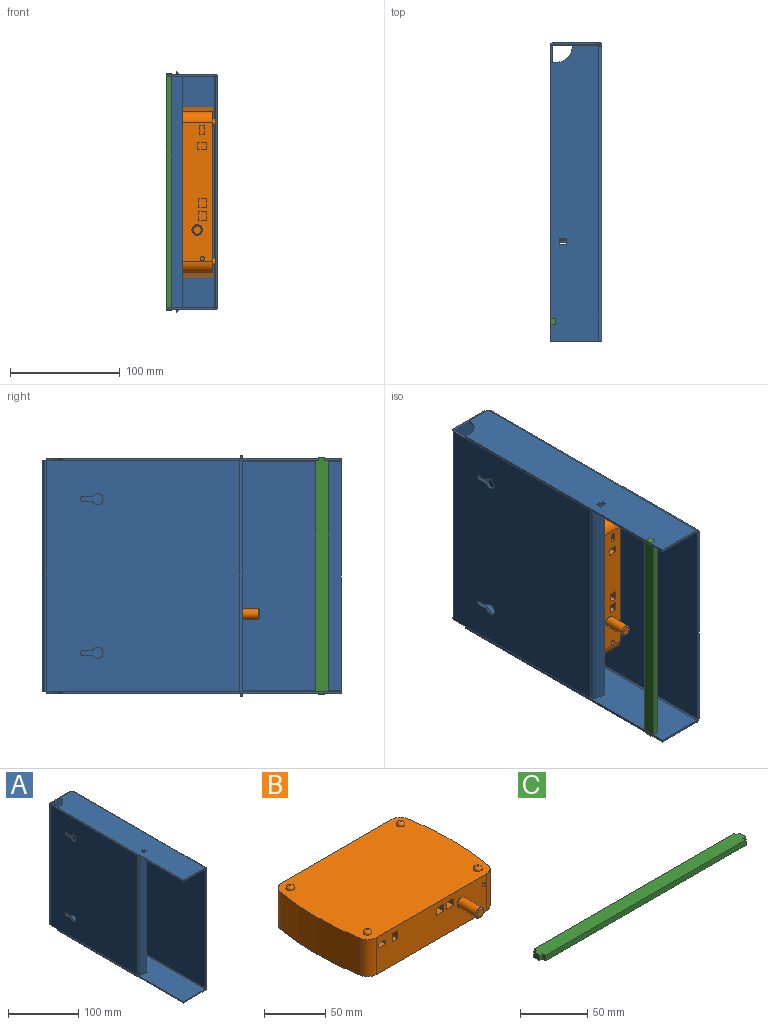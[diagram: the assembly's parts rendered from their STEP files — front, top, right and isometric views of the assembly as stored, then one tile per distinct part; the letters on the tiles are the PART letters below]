
ASSEMBLY  parts=3 mates=4
PART A: 83 faces, bbox 47x272x220 mm
  f0: plane 269x208mm, normal (1,0,0), area 55952.6mm2, adj f1,f3,f4,f49,f65,f81
  f1: plane 208x2mm, normal (0,-1,0), area 416mm2, adj f0,f2,f63,f79
  f2: plane 269x208mm, normal (-1,0,0), area 55952.6mm2, adj f1,f3,f4,f50,f66,f82
  f3: cylinder r=2.5mm len=2mm, axis (-1,0,0), area 1.5mm2, adj f0,f2,f47,f80
  f4: cylinder r=2.5mm len=2mm, axis (-1,0,0), area 1.5mm2, adj f0,f2,f48,f64
  f5: plane 40.04x2mm, normal (0,0,1), area 80.1mm2, adj f7,f11,f12,f44
  f6: plane 40.04x2mm, normal (0,0,-1), area 80.1mm2, adj f7,f11,f13,f43
  f7: plane 210x41mm, normal (0,1,0), area 8078mm2, adj f5,f6,f8,f9,f10,f12,f13,f45
  f8: cylinder r=7.5mm len=15mm, axis (0,1,0), area 94.2mm2, adj f7,f11
  f9: cylinder r=7.5mm len=15mm, axis (0,1,0), area 94.2mm2, adj f7,f11
  f10: cylinder r=7.5mm len=15mm, axis (0,1,0), area 94.2mm2, adj f7,f11
  f11: plane 210x41mm, normal (0,-1,0), area 8078mm2, adj f5,f6,f8,f9,f10,f12,f13,f46
  f12: cylinder r=2.5mm len=2mm, axis (0,-1,0), area 3.7mm2, adj f5,f7,f11,f47
  f13: cylinder r=2.5mm len=2mm, axis (0,-1,0), area 3.7mm2, adj f6,f7,f11,f48
  f14: plane 6.88x2mm, normal (0,0,-1), area 13.8mm2, adj f15,f27,f28,f29
  f15: cylinder r=5mm len=3.57mm, axis (-1,0,0), area 8mm2, adj f14,f16,f28,f29
  f16: cylinder r=5mm len=10mm, axis (-1,0,0), area 47.3mm2, adj f15,f17,f28,f29
  f17: cylinder r=5mm len=3.57mm, axis (-1,0,0), area 8mm2, adj f16,f18,f28,f29
  f18: plane 6.78x2mm, normal (0,0,1), area 13.6mm2, adj f17,f27,f28,f29
  f19: plane 6.78x2mm, normal (0,0,-1), area 13.6mm2, adj f20,f26,f28,f29
  f20: cylinder r=5mm len=3.57mm, axis (-1,0,0), area 8mm2, adj f19,f21,f28,f29
  f21: cylinder r=5mm len=10mm, axis (-1,0,0), area 47.3mm2, adj f20,f22,f28,f29
  f22: cylinder r=5mm len=3.57mm, axis (-1,0,0), area 8mm2, adj f21,f23,f28,f29
  f23: plane 6.88x2mm, normal (0,0,1), area 13.8mm2, adj f22,f26,f28,f29
  f24: plane 176x2mm, normal (0,0,1), area 352mm2, adj f28,f29,f40,f44
  f25: plane 176x2mm, normal (0,0,-1), area 352mm2, adj f28,f29,f39,f43
  f26: cylinder r=2mm len=4mm, axis (-1,0,0), area 12.8mm2, adj f19,f23,f28,f29
  f27: cylinder r=2mm len=4mm, axis (-1,0,0), area 12.8mm2, adj f14,f18,f28,f29
  f28: plane 210x176mm, normal (-1,0,0), area 36713.9mm2, adj f14,f15,f16,f17,f18,f19,f20,f21
  f29: plane 210x176mm, normal (1,0,0), area 36713.9mm2, adj f14,f15,f16,f17,f18,f19,f20,f21
  f30: plane 5x2mm, normal (-1,0,0), area 10mm2, adj f31,f36,f37,f38
  f31: plane 6x5mm, normal (0.64,0,-0.77), area 15.6mm2, adj f30,f32,f37,f38
  f32: plane 210x2mm, normal (1,0,0), area 420mm2, adj f31,f33,f37,f38
  f33: plane 6x5mm, normal (0.64,0,0.77), area 15.6mm2, adj f32,f34,f37,f38
  f34: plane 5x2mm, normal (-1,0,0), area 10mm2, adj f33,f35,f37,f38
  f35: plane 6x2mm, normal (0,0,1), area 12mm2, adj f34,f37,f38,f40
  f36: plane 6x2mm, normal (0,0,-1), area 12mm2, adj f30,f37,f38,f39
  f37: plane 220x12mm, normal (0,-1,0), area 2550mm2, adj f30,f31,f32,f33,f34,f35,f36,f41
  f38: plane 220x12mm, normal (0,1,0), area 2550mm2, adj f30,f31,f32,f33,f34,f35,f36,f42
  f39: plane 3x3mm, normal (0,0,-1), area 6.3mm2, adj f25,f36,f41,f42
  f40: plane 3x3mm, normal (0,0,1), area 6.3mm2, adj f24,f35,f41,f42
  f41: cylinder r=3mm len=210mm, axis (0,0,-1), area 989.6mm2, adj f28,f37,f39,f40
  f42: cylinder r=1mm len=210mm, axis (0,0,-1), area 329.9mm2, adj f29,f38,f39,f40
  f43: plane 3x3mm, normal (0,0,-1), area 6.3mm2, adj f6,f25,f45,f46
  f44: plane 3x3mm, normal (0,0,1), area 6.3mm2, adj f5,f24,f45,f46
  f45: cylinder r=3mm len=210mm, axis (0,0,-1), area 989.6mm2, adj f7,f28,f43,f44
  f46: cylinder r=1mm len=210mm, axis (0,0,-1), area 329.9mm2, adj f11,f29,f43,f44
  f47: bspline ~3x3mm, area 6.7mm2, adj f3,f12,f49,f50
  f48: bspline ~3x3mm, area 6.7mm2, adj f4,f13,f49,f50
  f49: cylinder r=3mm len=206.97mm, axis (0,0,1), area 972.2mm2, adj f0,f7,f47,f48
  f50: cylinder r=1mm len=206.97mm, axis (0,0,1), area 324.1mm2, adj f2,f11,f47,f48
  f51: plane 23.49x2.04mm, normal (0,1,0), area 47mm2, adj f52,f59,f61,f62
  f52: plane 269x44.01mm, normal (0,0,-1), area 11550.5mm2, adj f51,f53,f54,f55,f56,f57,f58,f59
  f53: plane 7x2.01mm, normal (0,1,0), area 14mm2, adj f52,f54,f60,f61
  f54: plane 5x2mm, normal (-1,0,0), area 10mm2, adj f52,f53,f55,f61
  f55: plane 7x2.01mm, normal (0,-1,0), area 14mm2, adj f52,f54,f60,f61
  f56: plane 44.01x2.08mm, normal (0,-1,0), area 88mm2, adj f52,f57,f61,f63
  f57: plane 254x2mm, normal (-1,0,0), area 508mm2, adj f52,f56,f58,f61
  f58: plane 5x2.01mm, normal (0,1,0), area 10mm2, adj f52,f57,f59,f61
  f59: cylinder r=15mm len=15mm, axis (0,0,-1), area 47.1mm2, adj f51,f52,f58,f61
  f60: plane 5x2mm, normal (1,0,0), area 10mm2, adj f52,f53,f55,f61
  f61: plane 269x44.01mm, normal (0,0,1), area 11550.5mm2, adj f51,f53,f54,f55,f56,f57,f58,f59
  f62: cylinder r=2.5mm len=2mm, axis (0,0,1), area 1.5mm2, adj f51,f52,f61,f64
  f63: plane 3x3mm, normal (0,-1,0), area 6.3mm2, adj f1,f56,f65,f66
  f64: bspline ~3x3mm, area 6.7mm2, adj f4,f62,f65,f66
  f65: cylinder r=3mm len=268.49mm, axis (0,1,0), area 1262.2mm2, adj f0,f52,f63,f64
  f66: cylinder r=1mm len=268.49mm, axis (0,1,0), area 420.7mm2, adj f2,f61,f63,f64
  f67: plane 23.49x2.04mm, normal (0,1,0), area 47mm2, adj f68,f75,f77,f78
  f68: plane 269x44.01mm, normal (0,0,1), area 11550.5mm2, adj f67,f69,f70,f71,f72,f73,f74,f75
  f69: plane 7x2.01mm, normal (0,1,0), area 14mm2, adj f68,f70,f76,f77
  f70: plane 5x2mm, normal (1,0,0), area 10mm2, adj f68,f69,f71,f77
  f71: plane 7x2.01mm, normal (0,-1,0), area 14mm2, adj f68,f70,f76,f77
  f72: plane 5x2.01mm, normal (0,1,0), area 10mm2, adj f68,f73,f75,f77
  f73: plane 254x2mm, normal (-1,0,0), area 508mm2, adj f68,f72,f74,f77
  f74: plane 44.01x2.08mm, normal (0,-1,0), area 88mm2, adj f68,f73,f77,f79
  f75: cylinder r=15mm len=15mm, axis (0,0,1), area 47.1mm2, adj f67,f68,f72,f77
  f76: plane 5x2mm, normal (-1,0,0), area 10mm2, adj f68,f69,f71,f77
  f77: plane 269x44.01mm, normal (0,0,-1), area 11550.5mm2, adj f67,f69,f70,f71,f72,f73,f74,f75
  f78: cylinder r=2.5mm len=2mm, axis (0,0,-1), area 1.5mm2, adj f67,f68,f77,f80
  f79: plane 3x3mm, normal (0,-1,0), area 6.3mm2, adj f1,f74,f81,f82
  f80: bspline ~3x3mm, area 6.7mm2, adj f3,f78,f81,f82
  f81: cylinder r=3mm len=268.49mm, axis (0,1,0), area 1262.2mm2, adj f0,f68,f79,f80
  f82: cylinder r=1mm len=268.49mm, axis (0,1,0), area 420.7mm2, adj f2,f77,f79,f80
PART B: 43 faces, bbox 154.7x131x40 mm
  f0: plane 127.34x37mm, normal (0,-1,0), area 4431.4mm2, adj f4,f5,f8,f9,f10,f11,f12,f13
  f1: plane 127.34x37mm, normal (0,1,0), area 4711.4mm2, adj f2,f7,f8,f9
  f2: cylinder r=10mm len=37mm, axis (0,0,-1), area 519.7mm2, adj f1,f3,f8,f9
  f3: cylinder r=279.19mm len=92.31mm, axis (0,0,-1), area 3431.1mm2, adj f2,f4,f8,f9
  f4: cylinder r=10mm len=37mm, axis (0,0,-1), area 519.7mm2, adj f0,f3,f8,f9
  f5: cylinder r=10mm len=37mm, axis (0,0,-1), area 519.7mm2, adj f0,f6,f8,f9
  f6: cylinder r=279.19mm len=92.31mm, axis (0,0,-1), area 3431.1mm2, adj f5,f7,f8,f9
  f7: cylinder r=10mm len=37mm, axis (0,0,-1), area 519.7mm2, adj f1,f6,f8,f9
  f8: plane 154.74x109mm, normal (0,0,1), area 16268mm2, adj f0,f1,f2,f3,f4,f5,f6,f7
  f9: plane 154.74x109mm, normal (0,0,-1), area 16422mm2, adj f0,f1,f2,f3,f4,f5,f6,f7
  f10: plane 13x7.04mm, normal (-1,0,0), area 91.6mm2, adj f0,f11,f13,f14
  f11: plane 13x8.1mm, normal (0,0,-1), area 105.3mm2, adj f0,f10,f12,f14
  f12: plane 13x7.04mm, normal (1,0,0), area 91.6mm2, adj f0,f11,f13,f14
  f13: plane 13x8.1mm, normal (0,0,1), area 105.3mm2, adj f0,f10,f12,f14
  f14: plane 8.1x7.04mm, normal (0,-1,0), area 57mm2, adj f10,f11,f12,f13
  f15: plane 13x8.1mm, normal (-1,0,0), area 105.3mm2, adj f0,f16,f18,f19
  f16: plane 13x6.22mm, normal (0,0,-1), area 80.9mm2, adj f0,f15,f17,f19
  f17: plane 13x8.1mm, normal (1,0,0), area 105.3mm2, adj f0,f16,f18,f19
  f18: plane 13x6.22mm, normal (0,0,1), area 80.9mm2, adj f0,f15,f17,f19
  f19: plane 8.1x6.22mm, normal (0,-1,0), area 50.4mm2, adj f15,f16,f17,f18
  f20: plane 13x7.63mm, normal (0,0,1), area 99.2mm2, adj f0,f21,f23,f24
  f21: plane 13x4.46mm, normal (-1,0,0), area 58mm2, adj f0,f20,f22,f24
  f22: plane 13x7.63mm, normal (0,0,-1), area 99.2mm2, adj f0,f21,f23,f24
  f23: plane 13x4.46mm, normal (1,0,0), area 58mm2, adj f0,f20,f22,f24
  f24: plane 7.63x4.46mm, normal (0,-1,0), area 34mm2, adj f20,f21,f22,f23
  f25: plane 13x7.04mm, normal (-1,0,0), area 91.6mm2, adj f0,f26,f28,f29
  f26: plane 13x8.1mm, normal (0,0,-1), area 105.3mm2, adj f0,f25,f27,f29
  f27: plane 13x7.04mm, normal (1,0,0), area 91.6mm2, adj f0,f26,f28,f29
  f28: plane 13x8.1mm, normal (0,0,1), area 105.3mm2, adj f0,f25,f27,f29
  f29: plane 8.1x7.04mm, normal (0,-1,0), area 57mm2, adj f25,f26,f27,f28
  f30: cylinder r=1.83mm len=13mm, axis (0,-1,0), area 149.8mm2, adj f0,f31
  f31: plane 3.67x3.67mm, normal (0,-1,0), area 10.6mm2, adj f30
  f32: cylinder r=4.75mm len=21mm, axis (0,1,0), area 626.7mm2, adj f0,f42
  f33: plane 7.5x7.5mm, normal (0,-1,0), area 44.2mm2, adj f42
  f34: plane 1x1mm, normal (0,0,1), area 0.8mm2, adj f41
  f35: plane 1x1mm, normal (0,0,1), area 0.8mm2, adj f40
  f36: plane 1x1mm, normal (0,0,1), area 0.8mm2, adj f39
  f37: plane 1x1mm, normal (0,0,1), area 0.8mm2, adj f38
  f38: torus R=0.5mm, axis (0,0,1), area 71.4mm2, adj f8,f37
  f39: torus R=0.5mm, axis (0,0,1), area 71.4mm2, adj f8,f36
  f40: torus R=0.5mm, axis (0,0,1), area 71.4mm2, adj f8,f35
  f41: torus R=0.5mm, axis (0,0,1), area 71.4mm2, adj f8,f34
  f42: cone r=3.75mm half-angle=45deg, axis (0,1,0), area 37.8mm2, adj f32,f33
PART C: 14 faces, bbox 216x12x5 mm
  f0: plane 5x3mm, normal (0,-1,0), area 15mm2, adj f1,f11,f12,f13
  f1: plane 5x3.5mm, normal (-1,0,0), area 17.5mm2, adj f0,f2,f12,f13
  f2: plane 210x5mm, normal (0,-1,0), area 1050mm2, adj f1,f3,f12,f13
  f3: plane 5x3.5mm, normal (1,0,0), area 17.5mm2, adj f2,f4,f12,f13
  f4: plane 5x3mm, normal (0,-1,0), area 15mm2, adj f3,f5,f12,f13
  f5: plane 6x5mm, normal (1,0,0), area 30mm2, adj f4,f6,f12,f13
  f6: plane 5x3mm, normal (0,1,0), area 15mm2, adj f5,f7,f12,f13
  f7: plane 5x2.5mm, normal (1,0,0), area 12.5mm2, adj f6,f8,f12,f13
  f8: plane 210x5mm, normal (0,1,0), area 1050mm2, adj f7,f9,f12,f13
  f9: plane 5x2.5mm, normal (-1,0,0), area 12.5mm2, adj f8,f10,f12,f13
  f10: plane 5x3mm, normal (0,1,0), area 15mm2, adj f9,f11,f12,f13
  f11: plane 6x5mm, normal (-1,0,0), area 30mm2, adj f0,f10,f12,f13
  f12: plane 216x12mm, normal (0,0,1), area 2556mm2, adj f0,f1,f2,f3,f4,f5,f6,f7
  f13: plane 216x12mm, normal (0,0,-1), area 2556mm2, adj f0,f1,f2,f3,f4,f5,f6,f7
PLACE A t=(100.38,-91.91,-104.7)mm fixed
PLACE B rot(axis=(0,1,0),90deg) t=(60.38,4.82,77.8)mm
PLACE C rot(axis=(0,1,0),89.9deg) t=(55.01,-80.41,105.22)mm
MATE planar A.f57 <-> C.f13  axis (-1,0,0) through (55.38,35.09,-105.78)mm
MATE parallel A.f10 <-> B.f1  axis (0,1,0) through (78.88,180.09,0.3)mm
MATE planar C.f3 <-> A.f61  axis (0,0,-1) through (57.88,-78.66,-104.78)mm
MATE planar A.f2 <-> B.f34  axis (-1,0,0) through (100.38,42.59,0.3)mm
